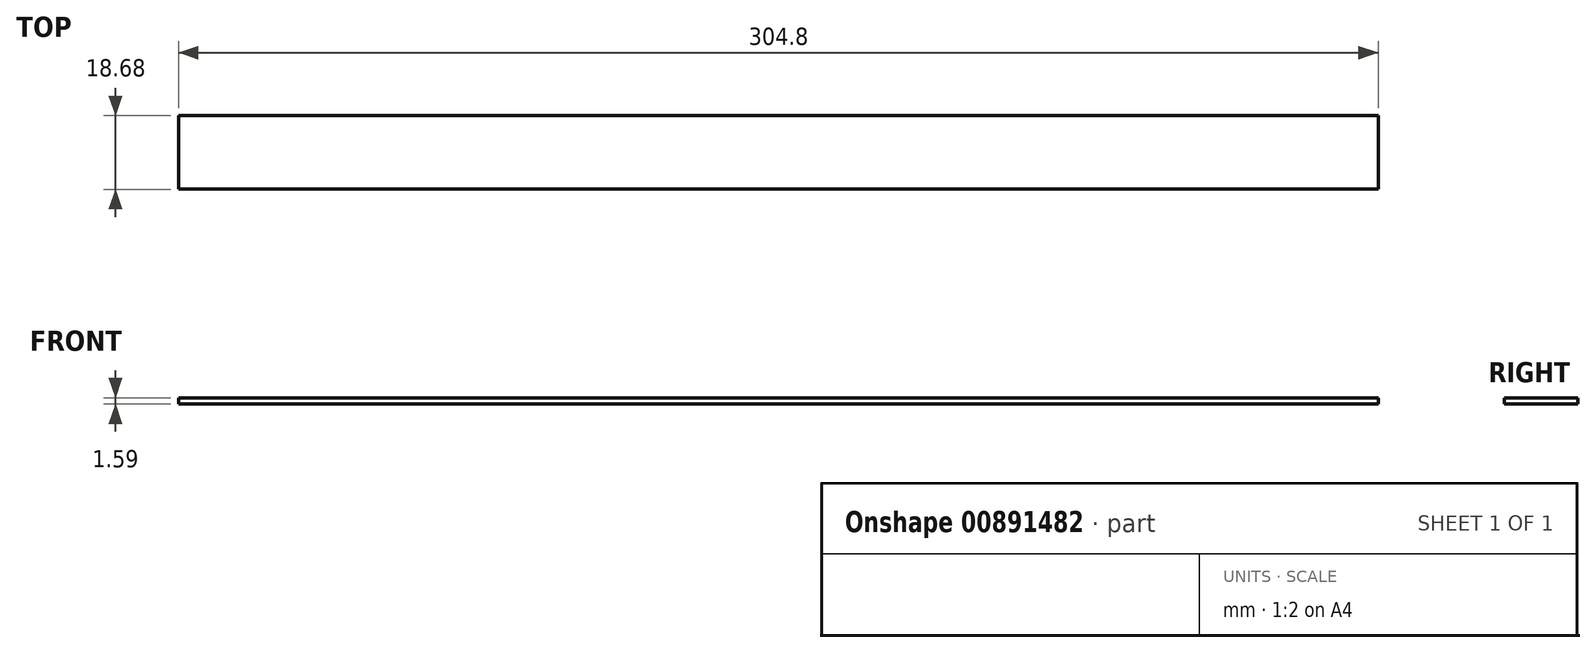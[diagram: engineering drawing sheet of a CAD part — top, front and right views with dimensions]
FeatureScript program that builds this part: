
annotation { "Feature Type Name" : "Feature", "Feature Type Description" : "" }
export const myFeature = defineFeature(function(context is Context, id is Id, definition is map)
    precondition{}
    {
        {
            var Q0;
            Q0=qCreatedBy(makeId("Top.planeOp"),FACE);
            var sketch = newSketch(context, id + "F0", { "sketchPlane" : qUnion([Q0])});
            skLineSegment(sketch, "E0.bottom", {"start": v(152.4, 9.34) * mm, "end": v(-152.4, 9.34) * mm});
            skLineSegment(sketch, "E0.top", {"start": v(152.4, -9.34) * mm, "end": v(-152.4, -9.34) * mm});
            skLineSegment(sketch, "E0.left", {"start": v(152.4, 9.34) * mm, "end": v(152.4, -9.34) * mm});
            skLineSegment(sketch, "E0.right", {"start": v(-152.4, 9.34) * mm, "end": v(-152.4, -9.34) * mm});
            skPoint(sketch, "E0.middle", {"position": v(0, 0) * mm});
            skSolve(sketch);
        }
        {
            var Q0;
            Q0=makeQuery(id+"F0.imprint","IMPRINT",FACE,{"disambiguationData":[TD([[makeQuery(id+"F0.imprint","IMPRINT",EDGE,{"derivedFrom":sQuery(id+"F0.wireOp",EDGE,"E0.bottom")}),1.0]])]});
            extrude(context, id + "F1", {"entities" : qUnion([Q0]), "depth" : 1.59 * mm, "offsetDistance" : 25 * mm});
        }
    });
